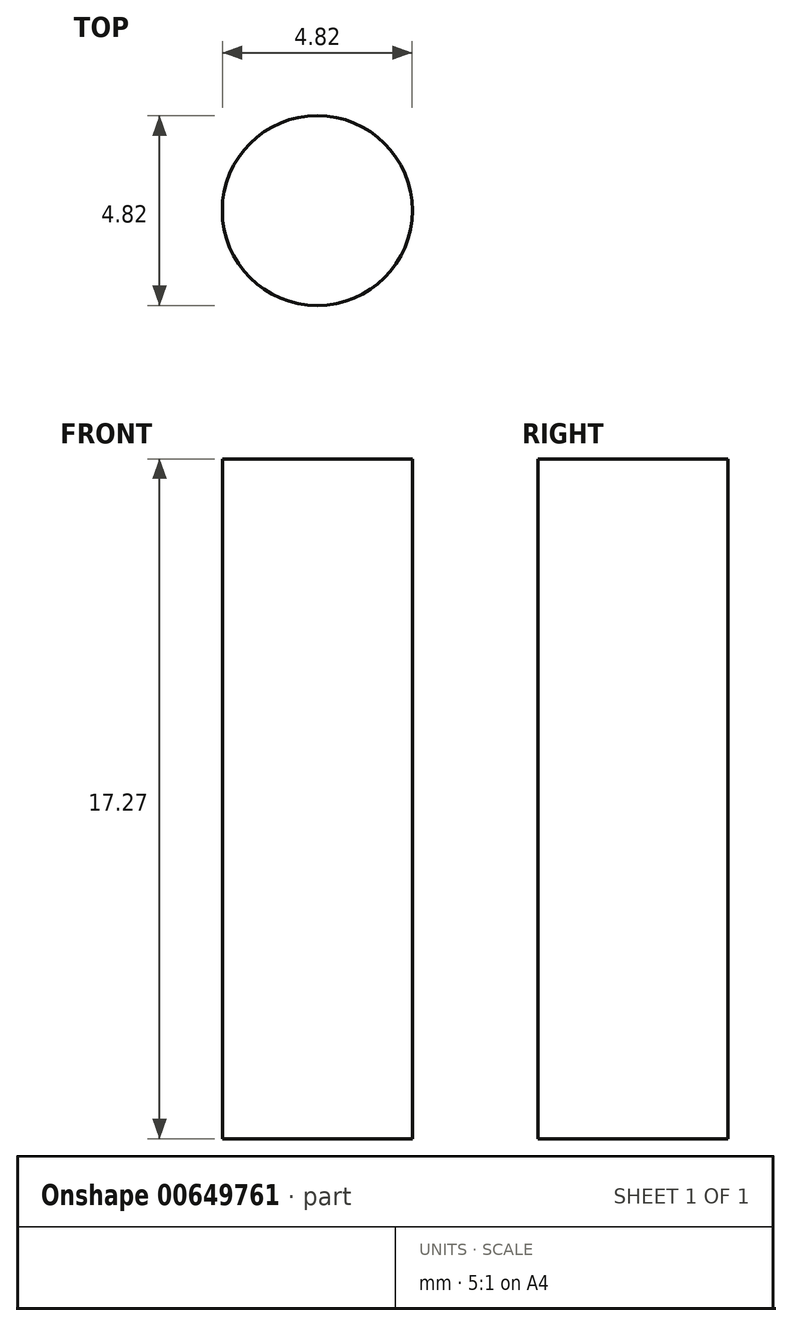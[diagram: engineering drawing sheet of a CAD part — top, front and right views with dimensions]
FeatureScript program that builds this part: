
annotation { "Feature Type Name" : "Feature", "Feature Type Description" : "" }
export const myFeature = defineFeature(function(context is Context, id is Id, definition is map)
    precondition{}
    {
        {
            var Q0;
            Q0=qCreatedBy(makeId("Top.planeOp"),FACE);
            var sketch = newSketch(context, id + "F0", { "sketchPlane" : qUnion([Q0])});
            skCircle(sketch, "E0", {"center": v(0, 0) * mm, "radius": 2.41 * mm});
            skSolve(sketch);
        }
        {
            var Q0;
            Q0=makeQuery(id+"F0.imprint","IMPRINT",FACE,{"disambiguationData":[TD([[makeQuery(id+"F0.imprint","IMPRINT",EDGE,{"derivedFrom":sQuery(id+"F0.wireOp",EDGE,"E0")}),1.0]])]});
            extrude(context, id + "F1", {"entities" : qUnion([Q0]), "depth" : 17.27 * mm, "offsetDistance" : 25.4 * mm});
        }
    });
